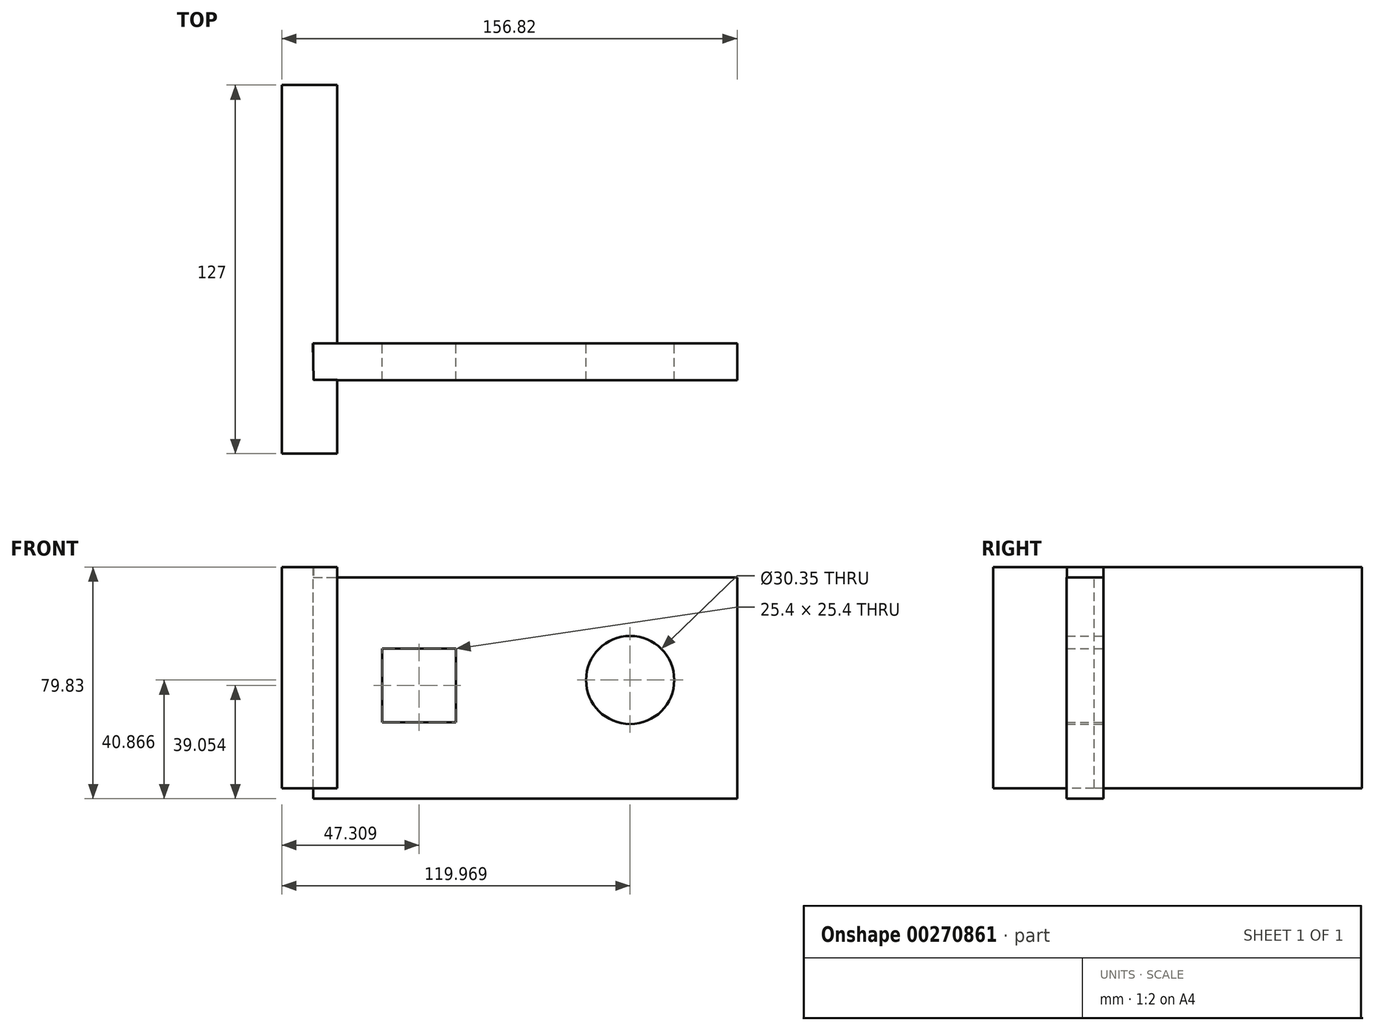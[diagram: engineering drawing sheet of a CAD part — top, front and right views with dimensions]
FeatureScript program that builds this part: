
annotation { "Feature Type Name" : "Feature", "Feature Type Description" : "" }
export const myFeature = defineFeature(function(context is Context, id is Id, definition is map)
    precondition{}
    {
        {
            var Q0;
            Q0=qCreatedBy(makeId("Front.planeOp"),FACE);
            var sketch = newSketch(context, id + "F0", { "sketchPlane" : qUnion([Q0])});
            skLineSegment(sketch, "E0.bottom", {"start": v(-89.34, 72.57) * mm, "end": v(56.71, 72.57) * mm});
            skLineSegment(sketch, "E0.top", {"start": v(-89.34, -3.63) * mm, "end": v(56.71, -3.63) * mm});
            skLineSegment(sketch, "E0.left", {"start": v(-89.34, 72.57) * mm, "end": v(-89.34, -3.63) * mm});
            skLineSegment(sketch, "E0.right", {"start": v(56.71, 72.57) * mm, "end": v(56.71, -3.63) * mm});
            skLineSegment(sketch, "E1.bottom", {"start": v(-65.5, 48.12) * mm, "end": v(-40.1, 48.12) * mm});
            skLineSegment(sketch, "E1.top", {"start": v(-65.5, 22.72) * mm, "end": v(-40.1, 22.72) * mm});
            skLineSegment(sketch, "E1.left", {"start": v(-65.5, 48.12) * mm, "end": v(-65.5, 22.72) * mm});
            skLineSegment(sketch, "E1.right", {"start": v(-40.1, 48.12) * mm, "end": v(-40.1, 22.72) * mm});
            skCircle(sketch, "E2", {"center": v(19.86, 37.24) * mm, "radius": 15.18 * mm});
            skSolve(sketch);
        }
        {
            var Q0;
            Q0=makeQuery(id+"F0.imprint","IMPRINT",FACE,{"disambiguationData":[TD([[makeQuery(id+"F0.imprint","IMPRINT",EDGE,{"derivedFrom":sQuery(id+"F0.wireOp",EDGE,"E0.bottom")}),-1.0]])]});
            extrude(context, id + "F1", {"entities" : qUnion([Q0]), "depth" : 12.7 * mm});
        }
        {
            var Q0;
            Q0=qCreatedBy(makeId("Top.planeOp"),FACE);
            var sketch = newSketch(context, id + "F2", { "sketchPlane" : qUnion([Q0])});
            skLineSegment(sketch, "E3", {"start": v(-81.06, -38.07) * mm, "end": v(-81.06, -12.67) * mm});
            skLineSegment(sketch, "E4", {"start": v(-81.06, -38.07) * mm, "end": v(-100.11, -38.07) * mm});
            skLineSegment(sketch, "E5", {"start": v(-100.11, -38.07) * mm, "end": v(-100.11, 88.93) * mm});
            skLineSegment(sketch, "E6", {"start": v(-81.06, 88.93) * mm, "end": v(-100.11, 88.93) * mm});
            skLineSegment(sketch, "E7", {"start": v(-81.06, 88.93) * mm, "end": v(-81.06, 0) * mm});
            skLineSegment(sketch, "E8", {"start": v(-81.06, 0) * mm, "end": v(-89.4, 0) * mm});
            skLineSegment(sketch, "E9", {"start": v(-81.06, -12.67) * mm, "end": v(-89.16, -12.67) * mm});
            skLineSegment(sketch, "E10", {"start": v(-89.4, 0) * mm, "end": v(-89.16, -12.67) * mm});
            skSolve(sketch);
        }
        {
            var Q0;
            Q0 = qSketchRegion(id + "F2", true);
            extrude(context, id + "F3", {"entities" : qUnion([Q0]), "operationType" : NewBodyOperationType.ADD, "depth" : 76.2 * mm});
        }
    });
